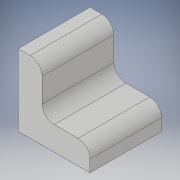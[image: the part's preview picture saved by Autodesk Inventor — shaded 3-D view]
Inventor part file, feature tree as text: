
AUTODESK INVENTOR PART (.ipt)
format: ipt  version: 2017 (Build 210142000, 142)  size: 103,936 bytes
history: native  units: in
note: dims shown in document units (in); Inventor stores cm internally (conversion verified against a paired STEP export)
features: fillet x2, extrude x1, sketch x1
ambient origin geometry x8: Origin, YZ Plane, XZ Plane, XY Plane, X Axis, Y Axis, Z Axis, Center Point
bodies: Solid1 (feature_tree)
feature tree (4):
  extrude  "Extrusion1"  Depth=0.5in
  fillet  "Fillet1"  Radius=1.0in
  fillet  "Fillet2"  Radius=1.0in
  sketch  "Sketch1"  dims[d0=1.5in d1=0.5in d2=1.0in d3=1.0in d4=1.5in d5=0.0in d6=0.25in d7=0.25in]
